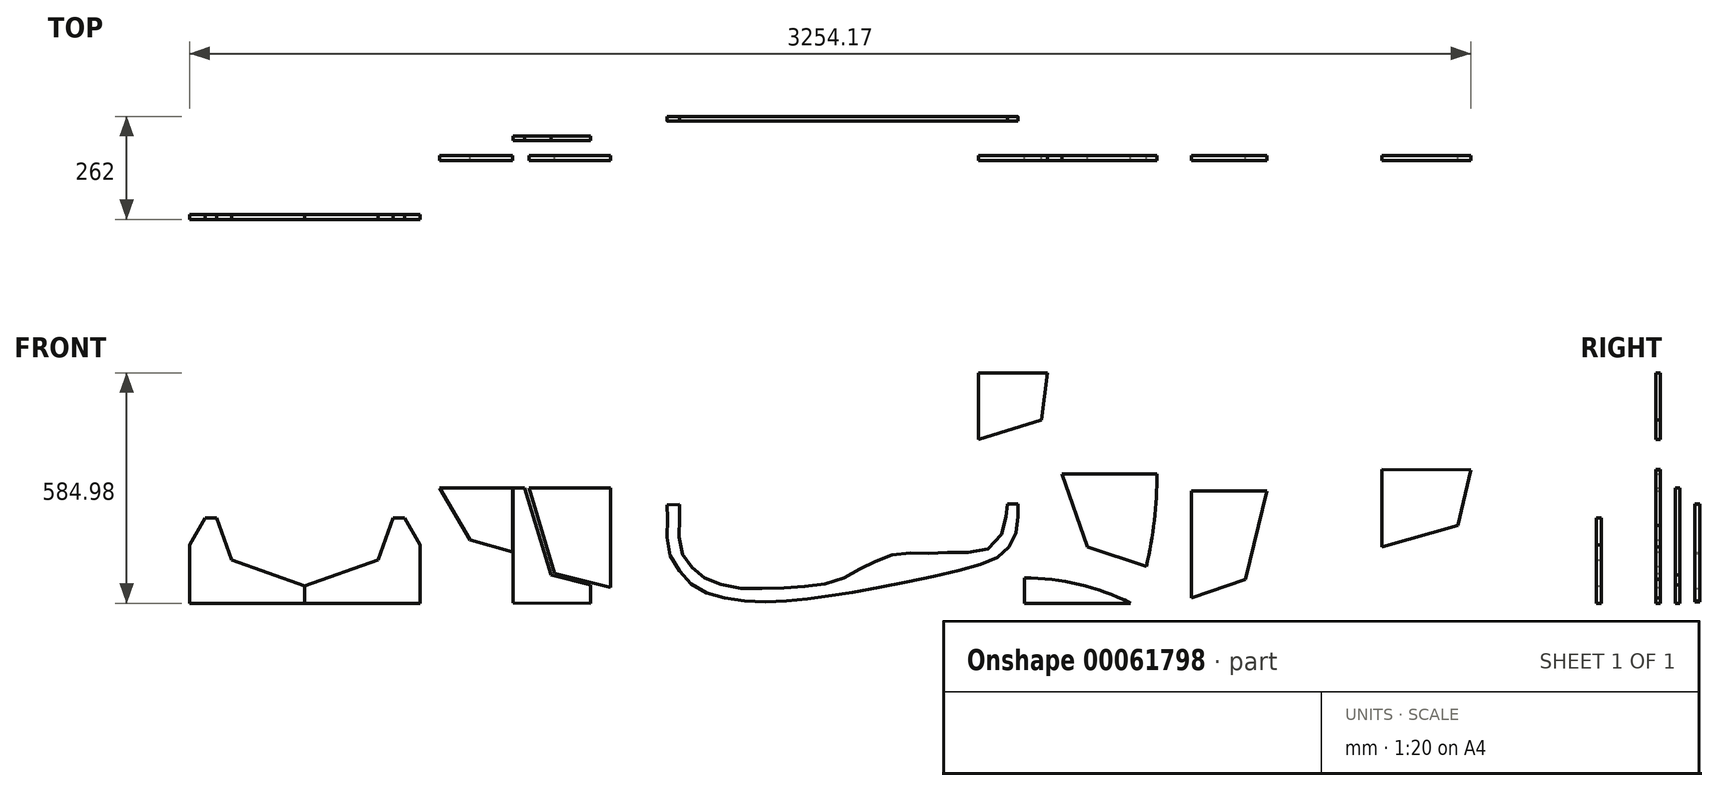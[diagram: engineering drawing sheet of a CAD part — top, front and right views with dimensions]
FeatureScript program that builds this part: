
annotation { "Feature Type Name" : "Feature", "Feature Type Description" : "" }
export const myFeature = defineFeature(function(context is Context, id is Id, definition is map)
    precondition{}
    {
        {
            var Q0;
            Q0=qCreatedBy(makeId("Front.planeOp"),FACE);
            var sketch = newSketch(context, id + "F0", { "sketchPlane" : qUnion([Q0])});
            skFitSpline(sketch, "E0", {"points": [v(-2243.05, -25.44) * mm, v(-2243.98, -16.42) * mm, v(-2246.04, 3.74) * mm, v(-2251.73, 34.57) * mm, v(-2266.06, 64.55) * mm, v(-2293.47, 88.88) * mm, v(-2331.78, 97.5) * mm, v(-2372.4, 97.43) * mm, v(-2409.6, 97.4) * mm, v(-2443.78, 98.85) * mm, v(-2475.9, 98) * mm, v(-2507.54, 98.78) * mm, v(-2539.43, 102.87) * mm, v(-2567.19, 113.88) * mm, v(-2593.9, 125.33) * mm, v(-2619.6, 138.39) * mm, v(-2646.1, 154.9) * mm, v(-2679.7, 166.64) * mm, v(-2715.61, 176.71) * mm, v(-2755.29, 181.36) * mm, v(-2796.14, 183.32) * mm, v(-2840.6, 186.3) * mm, v(-2884.66, 185.2) * mm, v(-2926.7, 185.18) * mm, v(-2964.32, 176.66) * mm, v(-2996.14, 167.64) * mm, v(-3021.51, 153.5) * mm, v(-3040.18, 137.61) * mm, v(-3054.54, 117.9) * mm, v(-3069.45, 97.34) * mm, v(-3077.28, 68.64) * mm, v(-3077.17, 34.43) * mm, v(-3076.08, 1.24) * mm, v(-3075.87, -20.2) * mm, v(-3075.79, -28.7) * mm]});
            skFitSpline(sketch, "E1", {"points": [v(-3106.85, -28.36) * mm, v(-3106.9, -20.44) * mm, v(-3107.02, 0.37) * mm, v(-3106.23, 31.69) * mm, v(-3108.31, 64.14) * mm, v(-3102.94, 93.46) * mm, v(-3090.77, 119.35) * mm, v(-3074.24, 143.6) * mm, v(-3056.37, 165.93) * mm, v(-3033.66, 182.62) * mm, v(-3008.83, 196.33) * mm, v(-2979, 205.88) * mm, v(-2944.71, 211.74) * mm, v(-2906.9, 217.31) * mm, v(-2868.34, 219.82) * mm, v(-2828.97, 218.22) * mm, v(-2789.58, 217.82) * mm, v(-2750, 212.56) * mm, v(-2710.29, 207.3) * mm, v(-2660.36, 200.6) * mm, v(-2601.7, 191.4) * mm, v(-2530.97, 177.85) * mm, v(-2463.88, 164.78) * mm, v(-2399.77, 150.4) * mm, v(-2347.33, 138.38) * mm, v(-2306.06, 126) * mm, v(-2276.88, 114.24) * mm, v(-2255.8, 102.32) * mm, v(-2242.01, 87.43) * mm, v(-2230.57, 71.2) * mm, v(-2221.96, 50.11) * mm, v(-2216.99, 25.98) * mm, v(-2216.73, -0.15) * mm, v(-2216.48, -16.5) * mm, v(-2216.34, -25.35) * mm]});
            skLineSegment(sketch, "E2", {"start": v(-2243.05, -25.44) * mm, "end": v(-2216.34, -25.35) * mm});
            skFitSpline(sketch, "E3", {"points": [v(-2243.05, -25.44) * mm, v(-2243.92, -34.46) * mm, v(-2245.85, -54.63) * mm, v(-2251.34, -85.5) * mm, v(-2265.47, -115.57) * mm, v(-2292.73, -140.08) * mm, v(-2330.98, -148.96) * mm, v(-2371.6, -149.14) * mm, v(-2408.8, -149.35) * mm, v(-2442.96, -151.02) * mm, v(-2475.1, -150.38) * mm, v(-2506.73, -151.37) * mm, v(-2538.59, -155.66) * mm, v(-2566.28, -166.86) * mm, v(-2592.9, -178.47) * mm, v(-2618.54, -191.7) * mm, v(-2644.93, -208.4) * mm, v(-2678.45, -220.34) * mm, v(-2714.3, -230.65) * mm, v(-2753.93, -235.55) * mm, v(-2794.77, -237.78) * mm, v(-2839.22, -241.05) * mm, v(-2883.28, -240.24) * mm, v(-2925.32, -240.48) * mm, v(-2963, -232.2) * mm, v(-2994.87, -223.4) * mm, v(-3020.34, -209.42) * mm, v(-3039.1, -193.65) * mm, v(-3053.59, -174.03) * mm, v(-3068.64, -153.57) * mm, v(-3076.65, -124.92) * mm, v(-3076.77, -90.71) * mm, v(-3075.9, -57.52) * mm, v(-3075.82, -36.07) * mm, v(-3075.8, -27.58) * mm]});
            skFitSpline(sketch, "E4", {"points": [v(-3106.85, -28.36) * mm, v(-3106.84, -36.2) * mm, v(-3106.83, -56.93) * mm, v(-3105.84, -88.16) * mm, v(-3107.71, -120.62) * mm, v(-3102.15, -149.91) * mm, v(-3089.8, -175.72) * mm, v(-3073.13, -199.87) * mm, v(-3055.1, -222.07) * mm, v(-3032.3, -238.62) * mm, v(-3007.38, -252.17) * mm, v(-2977.5, -261.52) * mm, v(-2943.16, -267.16) * mm, v(-2905.31, -272.49) * mm, v(-2866.73, -274.75) * mm, v(-2827.37, -272.89) * mm, v(-2787.99, -272.23) * mm, v(-2748.44, -266.72) * mm, v(-2708.77, -261.2) * mm, v(-2658.88, -254.18) * mm, v(-2600.29, -244.6) * mm, v(-2529.65, -230.59) * mm, v(-2462.65, -217.08) * mm, v(-2398.62, -202.29) * mm, v(-2346.26, -189.92) * mm, v(-2305.08, -177.28) * mm, v(-2275.98, -165.33) * mm, v(-2254.96, -153.28) * mm, v(-2241.28, -138.3) * mm, v(-2229.94, -121.98) * mm, v(-2221.47, -100.85) * mm, v(-2216.66, -76.68) * mm, v(-2216.56, -50.55) * mm, v(-2216.42, -34.2) * mm, v(-2216.34, -25.35) * mm]});
            skLineSegment(sketch, "E5", {"start": v(-3106.85, -28.24) * mm, "end": v(-3106.85, -28.36) * mm});
            skLineSegment(sketch, "E6", {"start": v(-3075.8, -28.14) * mm, "end": v(-3106.85, -28.24) * mm});
            skFitSpline(sketch, "E7", {"points": [v(-2118.13, -166.73) * mm, v(-2132.6, -165.65) * mm, v(-2163.36, -163.34) * mm, v(-2179.13, -136.51) * mm, v(-2187.5, -122.3) * mm]});
            skLineSegment(sketch, "E8", {"start": v(-2187.5, -122.3) * mm, "end": v(-2223.52, 127.42) * mm});
            skFitSpline(sketch, "E9", {"points": [v(-2223.52, 127.42) * mm, v(-2224.23, 132.93) * mm, v(-2226, 146.5) * mm, v(-2208.7, 163.68) * mm, v(-2183.27, 173.92) * mm, v(-2148.18, 166.6) * mm, v(-2133.18, 134.42) * mm, v(-2123.45, 113.8) * mm, v(-2121.76, 103.7) * mm]});
            skLineSegment(sketch, "E10", {"start": v(-2121.06, 96.9) * mm, "end": v(-2118.13, -166.73) * mm});
            skLineSegment(sketch, "E11", {"start": v(-2215.07, 72.49) * mm, "end": v(-2191.1, 76.68) * mm});
            skLineSegment(sketch, "E12", {"start": v(-2121.06, 96.9) * mm, "end": v(-2159.56, 113.17) * mm});
            skLineSegment(sketch, "E13", {"start": v(-3587.98, 306.96) * mm, "end": v(-3517.12, 274.88) * mm});
            skLineSegment(sketch, "E14", {"start": v(-3517.12, 274.88) * mm, "end": v(-3517.23, 240.88) * mm});
            skLineSegment(sketch, "E15", {"start": v(-3517.23, 240.88) * mm, "end": v(-3626.36, 201.24) * mm});
            skLineSegment(sketch, "E16", {"start": v(-3626.36, 201.24) * mm, "end": v(-3690.99, 14.46) * mm});
            skLineSegment(sketch, "E17", {"start": v(-3690.99, 14.46) * mm, "end": v(-3625.6, -171.76) * mm});
            skLineSegment(sketch, "E18", {"start": v(-3625.6, -171.76) * mm, "end": v(-3518.74, -210.12) * mm});
            skLineSegment(sketch, "E19", {"start": v(-3518.74, -210.12) * mm, "end": v(-3518.83, -239.12) * mm});
            skLineSegment(sketch, "E20", {"start": v(-3518.83, -239.12) * mm, "end": v(-3587, -278.04) * mm});
            skLineSegment(sketch, "E21", {"start": v(-3587, -278.04) * mm, "end": v(-3735, -278.04) * mm});
            skLineSegment(sketch, "E22", {"start": v(-3735, -278.04) * mm, "end": v(-3735, 306.96) * mm});
            skLineSegment(sketch, "E23", {"start": v(-3301.27, 306.96) * mm, "end": v(-3300.34, 262.64) * mm});
            skLineSegment(sketch, "E24", {"start": v(-3300.34, 262.64) * mm, "end": v(-3402.47, 236.14) * mm});
            skLineSegment(sketch, "E25", {"start": v(-3402.47, 236.14) * mm, "end": v(-3469.54, 14.46) * mm});
            skLineSegment(sketch, "E26", {"start": v(-3469.54, 14.46) * mm, "end": v(-3401.6, -206.87) * mm});
            skLineSegment(sketch, "E27", {"start": v(-3401.6, -206.87) * mm, "end": v(-3301.73, -231.36) * mm});
            skLineSegment(sketch, "E28", {"start": v(-3301.73, -231.36) * mm, "end": v(-3301.02, -278.04) * mm});
            skLineSegment(sketch, "E29", {"start": v(-3281.23, -278.04) * mm, "end": v(-3479.22, -278.04) * mm});
            skLineSegment(sketch, "E30", {"start": v(-3499.02, -278.04) * mm, "end": v(-3499.08, 306.96) * mm});
            skLineSegment(sketch, "E31", {"start": v(-3499.36, 177.32) * mm, "end": v(-3499.36, -147.69) * mm});
            skLineSegment(sketch, "E32", {"start": v(-3685.36, 14.46) * mm, "end": v(-3607.55, 146.98) * mm});
            skLineSegment(sketch, "E33", {"start": v(-3607.55, 146.98) * mm, "end": v(-3499.36, 177.32) * mm});
            skLineSegment(sketch, "E34", {"start": v(-1775.17, -264.74) * mm, "end": v(-1775.34, 276.26) * mm});
            skLineSegment(sketch, "E35", {"start": v(-1775.17, 279.14) * mm, "end": v(-1637.58, 231.47) * mm});
            skLineSegment(sketch, "E36", {"start": v(-1637.58, 231.47) * mm, "end": v(-1583.68, 7.2) * mm});
            skLineSegment(sketch, "E37", {"start": v(-2140.91, 306.94) * mm, "end": v(-2156.26, 187.98) * mm});
            skLineSegment(sketch, "E38", {"start": v(-2156.26, 187.98) * mm, "end": v(-2316.42, 137.46) * mm});
            skLineSegment(sketch, "E39", {"start": v(-1889.69, -184.8) * mm, "end": v(-2039, -135.3) * mm});
            skLineSegment(sketch, "E40", {"start": v(-2039, -135.3) * mm, "end": v(-2104.67, 50.15) * mm});
            skLineSegment(sketch, "E41", {"start": v(-2104.67, 50.15) * mm, "end": v(-2040.02, 236.76) * mm});
            skLineSegment(sketch, "E42", {"start": v(-2040.02, 236.76) * mm, "end": v(-1891.84, 291.48) * mm});
            skArc(sketch, "E43", {"start": v(-1889.69, -184.8) * mm, "mid": v(-1798.62, 53.76) * mm, "end": v(-1891.84, 291.48) * mm});
            skLineSegment(sketch, "E44", {"start": v(-3250.27, 267.57) * mm, "end": v(-3250.27, -237.5) * mm});
            skLineSegment(sketch, "E45", {"start": v(-3250.27, -237.5) * mm, "end": v(-3392.94, -202.5) * mm});
            skLineSegment(sketch, "E46", {"start": v(-3392.94, -202.5) * mm, "end": v(-3457.54, 14.46) * mm});
            skLineSegment(sketch, "E47", {"start": v(-3457.54, 14.46) * mm, "end": v(-3392.94, 231.11) * mm});
            skLineSegment(sketch, "E48", {"start": v(-3392.94, 231.11) * mm, "end": v(-3250.27, 267.57) * mm});
            skLineSegment(sketch, "E49", {"start": v(-1516.22, 61.56) * mm, "end": v(-1065.83, 60.97) * mm});
            skLineSegment(sketch, "E50", {"start": v(-1065.83, 60.97) * mm, "end": v(-1098.65, -80.85) * mm});
            skLineSegment(sketch, "E51", {"start": v(-1098.65, -80.85) * mm, "end": v(-1290.96, -134.75) * mm});
            skLineSegment(sketch, "E52", {"start": v(-3113.03, 106.96) * mm, "end": v(-3113.03, -278.04) * mm});
            skLineSegment(sketch, "E53", {"start": v(-3113.03, -278.04) * mm, "end": v(-3250.03, -278.04) * mm});
            skLineSegment(sketch, "E54", {"start": v(-3250.03, -278.04) * mm, "end": v(-3250.03, 106.96) * mm});
            skLineSegment(sketch, "E55", {"start": v(-3250.03, 106.96) * mm, "end": v(-3248.8, 303.96) * mm});
            skLineSegment(sketch, "E56", {"start": v(-3248.8, 303.96) * mm, "end": v(-3125.13, 282.94) * mm});
            skLineSegment(sketch, "E57", {"start": v(-3125.13, 282.94) * mm, "end": v(-3124.01, 106.9) * mm});
            skLineSegment(sketch, "E58", {"start": v(-3124.01, 106.9) * mm, "end": v(-3250.03, 106.96) * mm});
            skFitSpline(sketch, "E59", {"points": [v(-3021.64, -29.03) * mm, v(-3021.2, -69.2) * mm, v(-3020.56, -125.45) * mm, v(-2972.02, -206.62) * mm, v(-2881.38, -231.82) * mm, v(-2778.78, -224.88) * mm, v(-2675.77, -198.65) * mm, v(-2588.1, -154.63) * mm, v(-2538.66, -103.43) * mm, v(-2516.98, -61.68) * mm, v(-2515.58, -39.4) * mm, v(-2514.66, -24.67) * mm]});
            skFitSpline(sketch, "E60", {"points": [v(-3021.64, -29.03) * mm, v(-3021.88, 11.15) * mm, v(-3022.22, 67.4) * mm, v(-2975.07, 149.39) * mm, v(-2884.88, 176.14) * mm, v(-2782.18, 170.97) * mm, v(-2678.73, 146.51) * mm, v(-2590.32, 104) * mm, v(-2540, 53.66) * mm, v(-2517.61, 12.29) * mm, v(-2515.84, -9.97) * mm, v(-2514.66, -24.67) * mm]});
            skFitSpline(sketch, "E61", {"points": [v(-3046.82, -29.24) * mm, v(-3046.32, -73.39) * mm, v(-3045.63, -135.18) * mm, v(-2992.3, -224.35) * mm, v(-2892.72, -252.03) * mm, v(-2780, -244.41) * mm, v(-2666.83, -215.6) * mm, v(-2570.52, -167.23) * mm, v(-2516.2, -110.99) * mm, v(-2492.39, -65.12) * mm, v(-2490.85, -40.64) * mm, v(-2489.84, -24.46) * mm]});
            skFitSpline(sketch, "E62", {"points": [v(-3046.82, -29.24) * mm, v(-3047.08, 14.9) * mm, v(-3047.45, 76.7) * mm, v(-2995.66, 166.77) * mm, v(-2896.57, 196.16) * mm, v(-2783.74, 190.47) * mm, v(-2670.09, 163.6) * mm, v(-2572.96, 116.9) * mm, v(-2517.69, 61.6) * mm, v(-2493.08, 16.15) * mm, v(-2491.13, -8.3) * mm, v(-2489.84, -24.46) * mm]});
            skLineSegment(sketch, "E63", {"start": v(-3046.82, -29.24) * mm, "end": v(-3021.64, -29.03) * mm});
            skArc(sketch, "E64", {"start": v(-1889.69, -184.8) * mm, "mid": v(-1862.92, 53.42) * mm, "end": v(-1892.21, 291.35) * mm});
            skLineSegment(sketch, "E65", {"start": v(-3735, 306.96) * mm, "end": v(-1695, 306.96) * mm});
            skLineSegment(sketch, "E66", {"start": v(-2514.66, -24.67) * mm, "end": v(-2489.84, -24.46) * mm});
            skLineSegment(sketch, "E67", {"start": v(-2491.96, 305.02) * mm, "end": v(-2991.96, 305.02) * mm});
            skLineSegment(sketch, "E68", {"start": v(-2991.96, 305.02) * mm, "end": v(-2991.96, 255.02) * mm});
            skLineSegment(sketch, "E69", {"start": v(-1695, -278.04) * mm, "end": v(-3735, -278.04) * mm});
            skArc(sketch, "E70", {"start": v(-1929.84, -278.04) * mm, "mid": v(-2199.84, -167.1) * mm, "end": v(-2469.84, -278.04) * mm});
            skArc(sketch, "E71", {"start": v(-1929.84, -278.04) * mm, "mid": v(-2199.84, -213.86) * mm, "end": v(-2469.84, -278.04) * mm});
            skLineSegment(sketch, "E72", {"start": v(-3113.03, -158.04) * mm, "end": v(-3138.91, -158.04) * mm});
            skLineSegment(sketch, "E73", {"start": v(-3193.03, -198.04) * mm, "end": v(-3203.03, -198.04) * mm});
            skLineSegment(sketch, "E74", {"start": v(-3198.03, -203.04) * mm, "end": v(-3198.03, -193.04) * mm});
            skCircle(sketch, "E75", {"center": v(-3198.03, -198.04) * mm, "radius": 5 * mm});
            skFitSpline(sketch, "E76", {"points": [v(-3234.84, 85.11) * mm, v(-3220.4, 83.85) * mm, v(-3189.65, 81.16) * mm, v(-3174.21, 54.14) * mm, v(-3166.03, 39.82) * mm]});
            skLineSegment(sketch, "E77", {"start": v(-3166.03, 39.82) * mm, "end": v(-3133.08, -210.32) * mm});
            skFitSpline(sketch, "E78", {"points": [v(-3133.08, -210.32) * mm, v(-3132.43, -215.83) * mm, v(-3130.84, -229.42) * mm, v(-3148.34, -246.4) * mm, v(-3173.9, -256.32) * mm, v(-3208.9, -248.56) * mm, v(-3224, -215.06) * mm, v(-3235.93, -188.99) * mm, v(-3235.13, -172.6) * mm, v(-3234.9, -167.89) * mm]});
            skLineSegment(sketch, "E79", {"start": v(-3234.9, -167.89) * mm, "end": v(-3234.84, 85.11) * mm});
            skCircle(sketch, "E80", {"center": v(-2158.42, 115.95) * mm, "radius": 3 * mm});
            skLineSegment(sketch, "E81", {"start": v(-2121.76, 103.7) * mm, "end": v(-2157.28, 118.72) * mm});
            skLineSegment(sketch, "E82", {"start": v(-2158.42, 115.95) * mm, "end": v(-2159.38, 118.8) * mm});
            skLineSegment(sketch, "E83", {"start": v(-2159.38, 118.8) * mm, "end": v(-2158.42, 115.95) * mm});
            skLineSegment(sketch, "E84", {"start": v(-2158.42, 115.95) * mm, "end": v(-2157.46, 113.1) * mm});
            skLineSegment(sketch, "E85", {"start": v(-2157.46, 113.1) * mm, "end": v(-2158.42, 115.95) * mm});
            skLineSegment(sketch, "E86", {"start": v(-2158.42, 115.95) * mm, "end": v(-2161.26, 114.99) * mm});
            skLineSegment(sketch, "E87", {"start": v(-2161.26, 114.99) * mm, "end": v(-2158.42, 115.95) * mm});
            skLineSegment(sketch, "E88", {"start": v(-2158.42, 115.95) * mm, "end": v(-2155.58, 116.9) * mm});
            skLineSegment(sketch, "E89", {"start": v(-3250.03, 106.96) * mm, "end": v(-3113.03, 106.96) * mm});
            skLineSegment(sketch, "E90", {"start": v(-2491.96, 305.02) * mm, "end": v(-2491.96, 264.57) * mm});
            skFitSpline(sketch, "E91", {"points": [v(-1683.92, 291.86) * mm, v(-1647.43, 267.6) * mm, v(-1578.86, 222.03) * mm, v(-1477.55, 160.36) * mm, v(-1402, 129.5) * mm, v(-1361.26, 116.83) * mm, v(-1354.92, 114.86) * mm]});
            skFitSpline(sketch, "E92", {"points": [v(-1354.92, 114.86) * mm, v(-1327.92, 114.14) * mm, v(-1234.27, 111.67) * mm, v(-1073.9, 110.34) * mm, v(-873.92, 105.8) * mm, v(-673.93, 101.6) * mm, v(-473.91, 98.98) * mm, v(-273.92, 95.65) * mm, v(-73.89, 93.59) * mm, v(126.06, 87.15) * mm, v(292.11, 85.34) * mm, v(458.73, 79.4) * mm, v(625.47, 77.02) * mm, v(826.01, 67.34) * mm, v(1026.1, 66.83) * mm, v(1226.05, 60.51) * mm, v(1426.09, 62.27) * mm, v(1626.08, 61.55) * mm, v(1826.09, 62.67) * mm, v(2026.08, 64.93) * mm, v(2226.08, 66.77) * mm, v(2426.08, 69.14) * mm, v(2626.12, 69.8) * mm, v(2826.05, 76.78) * mm, v(3018.77, 78.17) * mm, v(3144.75, 81.36) * mm, v(3204.08, 82.86) * mm]});
            skLineSegment(sketch, "E93", {"start": v(3204.08, 82.86) * mm, "end": v(3717.08, 272.86) * mm});
            skFitSpline(sketch, "E94", {"points": [v(-1683.92, 291.86) * mm, v(-1647.27, 287.36) * mm, v(-1577.37, 278.77) * mm, v(-1473.95, 268.82) * mm, v(-1374, 259.47) * mm, v(-1240.71, 250.15) * mm, v(-1073.96, 244.28) * mm, v(-873.93, 240.72) * mm, v(-673.92, 237.98) * mm, v(-473.92, 234.51) * mm, v(-273.91, 233.12) * mm, v(-73.92, 230.16) * mm, v(126.09, 231.39) * mm, v(326.08, 229.44) * mm, v(526.08, 230.02) * mm, v(726.09, 229.64) * mm, v(926.08, 230.56) * mm, v(1126.1, 233.27) * mm, v(1326.08, 227.52) * mm, v(1526.08, 223.79) * mm, v(1726.12, 220.48) * mm, v(1926.06, 213.45) * mm, v(2126.08, 208.88) * mm, v(2326.06, 204.2) * mm, v(2526.09, 203.47) * mm, v(2720.8, 205.02) * mm, v(2887.5, 210.17) * mm, v(3054.06, 219.7) * mm, v(3192.84, 225.23) * mm, v(3326.17, 234.47) * mm, v(3489.83, 249.73) * mm, v(3620.1, 262.99) * mm, v(3717.08, 272.86) * mm]});
            skFitSpline(sketch, "E95", {"points": [v(-1453.62, -178.53) * mm, v(-1433.67, -185.01) * mm, v(-1397.35, -196.82) * mm, v(-1344.25, -211.67) * mm, v(-1277.2, -220.23) * mm, v(-1193.6, -221.95) * mm, v(-1093.67, -227.48) * mm, v(-993.6, -227.3) * mm, v(-860.29, -228.9) * mm, v(-726.95, -230.88) * mm, v(-560.28, -230.2) * mm, v(-393.6, -232.5) * mm, v(-193.61, -235.45) * mm, v(6.38, -238.87) * mm, v(206.39, -240.25) * mm, v(406.38, -243.3) * mm, v(606.39, -241.71) * mm, v(806.4, -245.03) * mm, v(1006.37, -239.36) * mm, v(1206.39, -240.72) * mm, v(1406.39, -240.93) * mm, v(1606.4, -238.74) * mm, v(1806.38, -235.28) * mm, v(2006.38, -233.3) * mm, v(2206.39, -232.69) * mm, v(2373.07, -231.4) * mm, v(2506.4, -228.55) * mm, v(2606.48, -226.31) * mm, v(2706.62, -219.36) * mm, v(2806.74, -207.3) * mm, v(2906.87, -190.33) * mm, v(2997.36, -170.15) * mm, v(3054.4, -155.63) * mm, v(3078.38, -149.53) * mm]});
            skFitSpline(sketch, "E96", {"points": [v(-1453.62, -178.53) * mm, v(-1400.3, -173.75) * mm, v(-1313.64, -165.98) * mm, v(-1193.4, -156.48) * mm, v(-1093.74, -142.81) * mm, v(-993.37, -133.47) * mm, v(-860.39, -113.38) * mm, v(-694.01, -90.19) * mm, v(-493.67, -70.6) * mm, v(-293.8, -50.65) * mm, v(-93.7, -36.07) * mm, v(106.3, -24.28) * mm, v(306.28, -14) * mm, v(506.39, -12.93) * mm, v(706.38, -9.47) * mm, v(906.4, -12.37) * mm, v(1106.5, -16.25) * mm, v(1306.37, -27.85) * mm, v(1506.38, -37.53) * mm, v(1706.44, -47.2) * mm, v(1906.5, -58.9) * mm, v(2106.42, -74.45) * mm, v(2306.39, -90.51) * mm, v(2506.35, -106.68) * mm, v(2706.33, -121.92) * mm, v(2897.15, -134.22) * mm, v(3021.06, -144.69) * mm, v(3078.38, -149.53) * mm]});
            skLineSegment(sketch, "E97", {"start": v(327.38, -242.53) * mm, "end": v(327.38, -169.52) * mm});
            skLineSegment(sketch, "E98", {"start": v(3725.24, -204.64) * mm, "end": v(3725.24, 295.36) * mm});
            skLineSegment(sketch, "E99", {"start": v(3646.25, -253.66) * mm, "end": v(3146.25, -253.66) * mm});
            skLineSegment(sketch, "E100", {"start": v(3725.24, -204.64) * mm, "end": v(3675.24, -204.64) * mm});
            skLineSegment(sketch, "E101", {"start": v(3146.25, -213.2) * mm, "end": v(3146.25, -253.66) * mm});
            skLineSegment(sketch, "E102", {"start": v(3646.25, -213.2) * mm, "end": v(3646.25, -253.66) * mm});
            skLineSegment(sketch, "E103", {"start": v(3725.24, 295.36) * mm, "end": v(3684.56, 295.36) * mm});
            skLineSegment(sketch, "E104", {"start": v(-1695, 306.96) * mm, "end": v(3735, 306.96) * mm});
            skLineSegment(sketch, "E105", {"start": v(3735, 306.96) * mm, "end": v(3735, -278.04) * mm});
            skLineSegment(sketch, "E106", {"start": v(-1695, -278.04) * mm, "end": v(3735, -278.04) * mm});
            skFitSpline(sketch, "E107", {"points": [v(-1572.01, 218.65) * mm, v(-1539.34, 215.11) * mm, v(-1473.32, 208.76) * mm, v(-1374, 199.47) * mm, v(-1240.71, 190.15) * mm, v(-1073.96, 184.28) * mm, v(-873.93, 180.72) * mm, v(-673.92, 177.98) * mm, v(-473.92, 174.51) * mm, v(-273.91, 173.12) * mm, v(-73.92, 170.16) * mm, v(126.09, 171.39) * mm, v(326.08, 169.44) * mm, v(526.08, 170.02) * mm, v(726.09, 169.64) * mm, v(926.08, 170.56) * mm, v(1126.1, 173.27) * mm, v(1326.08, 167.52) * mm, v(1526.08, 163.79) * mm, v(1726.12, 160.48) * mm, v(1926.06, 153.45) * mm, v(2126.08, 148.88) * mm, v(2326.06, 144.2) * mm, v(2526.09, 143.47) * mm, v(2720.8, 145.02) * mm, v(2887.5, 150.17) * mm, v(3054.06, 159.7) * mm, v(3192.84, 165.23) * mm, v(3326.17, 174.47) * mm, v(3415.66, 182.81) * mm, v(3471.85, 188.26) * mm, v(3494.73, 190.5) * mm]});
            skFitSpline(sketch, "E108", {"points": [v(-2958.87, -25.9) * mm, v(-2957.85, -5.92) * mm, v(-2955.23, 45.3) * mm, v(-2947.8, 110.6) * mm, v(-2918.5, 164.73) * mm, v(-2888.4, 188.06) * mm, v(-2859.34, 196.73) * mm, v(-2839.31, 201.13) * mm, v(-2819.37, 204.62) * mm, v(-2799.4, 207.18) * mm, v(-2779.38, 208.33) * mm, v(-2759.45, 210.04) * mm, v(-2739.37, 210.9) * mm, v(-2719.4, 208.6) * mm, v(-2699.2, 207.8) * mm, v(-2679.03, 204.02) * mm, v(-2658.79, 198.56) * mm, v(-2638.76, 190.8) * mm, v(-2618.55, 182.28) * mm, v(-2598.04, 172.88) * mm, v(-2577.79, 161.18) * mm, v(-2557.11, 147.68) * mm, v(-2536.6, 130.79) * mm, v(-2513.35, 108.8) * mm, v(-2485.75, 61.05) * mm, v(-2478.84, 16.62) * mm, v(-2474.01, -14.39) * mm]});
            skFitSpline(sketch, "E109", {"points": [v(-2978.96, -26.14) * mm, v(-2977.85, -4.5) * mm, v(-2975.01, 50.95) * mm, v(-2966.98, 121.62) * mm, v(-2935.25, 180.22) * mm, v(-2902.66, 205.48) * mm, v(-2871.21, 214.87) * mm, v(-2849.54, 219.63) * mm, v(-2827.95, 223.4) * mm, v(-2806.33, 226.17) * mm, v(-2784.66, 227.42) * mm, v(-2763.08, 229.27) * mm, v(-2741.34, 230.2) * mm, v(-2719.73, 227.7) * mm, v(-2697.85, 226.85) * mm, v(-2676.03, 222.76) * mm, v(-2654.1, 216.86) * mm, v(-2624.95, 205.47) * mm, v(-2595.25, 192.94) * mm, v(-2566.43, 176.4) * mm, v(-2544.05, 161.76) * mm, v(-2521.85, 143.48) * mm, v(-2496.68, 119.67) * mm, v(-2466.8, 68) * mm, v(-2459.32, 19.9) * mm, v(-2454.1, -13.67) * mm]});
            skFitSpline(sketch, "E110", {"points": [v(-2958.89, -25.42) * mm, v(-2956.91, -45.33) * mm, v(-2951.86, -96.38) * mm, v(-2941.35, -161.24) * mm, v(-2909.5, -213.93) * mm, v(-2878.32, -235.8) * mm, v(-2848.9, -243.09) * mm, v(-2828.68, -246.53) * mm, v(-2808.6, -249.06) * mm, v(-2788.53, -250.67) * mm, v(-2768.47, -250.87) * mm, v(-2748.48, -251.63) * mm, v(-2728.38, -251.54) * mm, v(-2708.55, -248.29) * mm, v(-2688.4, -246.54) * mm, v(-2668.44, -241.8) * mm, v(-2648.48, -235.4) * mm, v(-2628.85, -226.68) * mm, v(-2609.06, -217.21) * mm, v(-2589.02, -206.85) * mm, v(-2569.35, -194.2) * mm, v(-2549.33, -179.73) * mm, v(-2529.65, -161.9) * mm, v(-2507.47, -138.82) * mm, v(-2482.17, -89.82) * mm, v(-2477.37, -45.11) * mm, v(-2474.02, -13.9) * mm]});
            skFitSpline(sketch, "E111", {"points": [v(-2978.96, -26.14) * mm, v(-2976.83, -47.7) * mm, v(-2971.36, -102.96) * mm, v(-2959.98, -173.16) * mm, v(-2925.5, -230.2) * mm, v(-2891.75, -253.87) * mm, v(-2859.9, -261.76) * mm, v(-2838.01, -265.49) * mm, v(-2816.27, -268.23) * mm, v(-2794.55, -269.98) * mm, v(-2772.84, -270.19) * mm, v(-2751.2, -271.01) * mm, v(-2729.44, -270.91) * mm, v(-2707.97, -267.4) * mm, v(-2686.16, -265.5) * mm, v(-2664.55, -260.38) * mm, v(-2642.95, -253.43) * mm, v(-2621.7, -244) * mm, v(-2600.27, -233.76) * mm, v(-2578.58, -222.54) * mm, v(-2557.28, -208.85) * mm, v(-2535.62, -193.18) * mm, v(-2514.31, -173.87) * mm, v(-2490.3, -148.9) * mm, v(-2462.91, -95.85) * mm, v(-2457.72, -47.46) * mm, v(-2454.1, -13.67) * mm]});
            skFitSpline(sketch, "E112", {"points": [v(-1666.66, 280.4) * mm, v(-1634.9, 276.5) * mm, v(-1569.89, 268.63) * mm, v(-1471.38, 259.15) * mm, v(-1371.43, 249.8) * mm, v(-1238.14, 240.48) * mm, v(-1071.4, 234.61) * mm, v(-871.36, 231.06) * mm, v(-671.35, 228.31) * mm, v(-471.36, 224.85) * mm, v(-271.35, 223.45) * mm, v(-71.35, 220.5) * mm, v(128.65, 221.72) * mm, v(328.65, 219.77) * mm, v(528.65, 220.35) * mm, v(728.65, 219.98) * mm, v(928.65, 220.9) * mm, v(1128.68, 223.6) * mm, v(1328.65, 217.86) * mm, v(1528.65, 214.12) * mm, v(1728.68, 210.81) * mm, v(1928.63, 203.79) * mm, v(2128.64, 199.21) * mm, v(2328.63, 194.54) * mm, v(2528.66, 193.8) * mm, v(2723.36, 195.36) * mm, v(2890.06, 200.5) * mm, v(3056.63, 210.05) * mm, v(3195.41, 215.56) * mm, v(3328.74, 224.8) * mm, v(3479.21, 238.84) * mm, v(3596.33, 250.66) * mm, v(3680.14, 259.17) * mm]});
            skFitSpline(sketch, "E113", {"points": [v(-1646.96, 267.34) * mm, v(-1622.63, 264.39) * mm, v(-1565.02, 257.58) * mm, v(-1473.95, 248.82) * mm, v(-1374, 239.47) * mm, v(-1240.71, 230.15) * mm, v(-1073.96, 224.28) * mm, v(-873.93, 220.72) * mm, v(-673.92, 217.98) * mm, v(-473.92, 214.51) * mm, v(-273.91, 213.12) * mm, v(-73.92, 210.16) * mm, v(126.09, 211.39) * mm, v(326.08, 209.44) * mm, v(526.08, 210.02) * mm, v(726.09, 209.64) * mm, v(926.08, 210.56) * mm, v(1126.1, 213.27) * mm, v(1326.08, 207.52) * mm, v(1526.08, 203.79) * mm, v(1726.12, 200.48) * mm, v(1926.06, 193.45) * mm, v(2126.08, 188.88) * mm, v(2326.06, 184.2) * mm, v(2526.09, 183.47) * mm, v(2720.8, 185.02) * mm, v(2887.5, 190.17) * mm, v(3054.06, 199.7) * mm, v(3192.84, 205.23) * mm, v(3326.17, 214.47) * mm, v(3465, 227.42) * mm, v(3570.49, 237.98) * mm, v(3642.66, 245.3) * mm]});
            skFitSpline(sketch, "E114", {"points": [v(-1628.4, 255.1) * mm, v(-1610.25, 252.94) * mm, v(-1558.81, 246.98) * mm, v(-1473.95, 238.82) * mm, v(-1374, 229.47) * mm, v(-1240.71, 220.15) * mm, v(-1073.96, 214.28) * mm, v(-873.93, 210.72) * mm, v(-673.92, 207.98) * mm, v(-473.92, 204.51) * mm, v(-273.91, 203.12) * mm, v(-73.92, 200.16) * mm, v(126.09, 201.39) * mm, v(326.08, 199.44) * mm, v(526.08, 200.02) * mm, v(726.09, 199.64) * mm, v(926.08, 200.56) * mm, v(1126.1, 203.27) * mm, v(1326.08, 197.52) * mm, v(1526.08, 193.79) * mm, v(1726.12, 190.48) * mm, v(1926.06, 183.45) * mm, v(2126.08, 178.88) * mm, v(2326.06, 174.2) * mm, v(2526.09, 173.47) * mm, v(2720.8, 175.02) * mm, v(2887.5, 180.17) * mm, v(3054.06, 189.7) * mm, v(3192.84, 195.23) * mm, v(3326.17, 204.47) * mm, v(3452.61, 216.26) * mm, v(3545.73, 225.51) * mm, v(3605.53, 231.54) * mm]});
            skFitSpline(sketch, "E115", {"points": [v(-1609.75, 242.9) * mm, v(-1597.81, 241.51) * mm, v(-1552.58, 236.38) * mm, v(-1473.95, 228.82) * mm, v(-1374, 219.47) * mm, v(-1240.71, 210.15) * mm, v(-1073.96, 204.28) * mm, v(-873.93, 200.72) * mm, v(-673.92, 197.98) * mm, v(-473.92, 194.51) * mm, v(-273.91, 193.12) * mm, v(-73.92, 190.16) * mm, v(126.09, 191.39) * mm, v(326.08, 189.44) * mm, v(526.08, 190.02) * mm, v(726.09, 189.64) * mm, v(926.08, 190.56) * mm, v(1126.1, 193.27) * mm, v(1326.08, 187.52) * mm, v(1526.08, 183.79) * mm, v(1726.12, 180.48) * mm, v(1926.06, 173.45) * mm, v(2126.08, 168.88) * mm, v(2326.06, 164.2) * mm, v(2526.09, 163.47) * mm, v(2720.8, 165.02) * mm, v(2887.5, 170.17) * mm, v(3054.06, 179.7) * mm, v(3192.84, 185.23) * mm, v(3326.17, 194.47) * mm, v(3440.25, 205.1) * mm, v(3521.02, 213.07) * mm, v(3568.47, 217.82) * mm]});
            skFitSpline(sketch, "E116", {"points": [v(-1590.96, 230.75) * mm, v(-1585.28, 230.1) * mm, v(-1546.3, 225.78) * mm, v(-1473.95, 218.82) * mm, v(-1374, 209.47) * mm, v(-1240.71, 200.15) * mm, v(-1073.96, 194.28) * mm, v(-873.93, 190.72) * mm, v(-673.92, 187.98) * mm, v(-473.92, 184.51) * mm, v(-273.91, 183.12) * mm, v(-73.92, 180.16) * mm, v(126.09, 181.39) * mm, v(326.08, 179.44) * mm, v(526.08, 180.02) * mm, v(726.09, 179.64) * mm, v(926.08, 180.56) * mm, v(1126.1, 183.27) * mm, v(1326.08, 177.52) * mm, v(1526.08, 173.79) * mm, v(1726.12, 170.48) * mm, v(1926.06, 163.45) * mm, v(2126.08, 158.88) * mm, v(2326.06, 154.2) * mm, v(2526.09, 153.47) * mm, v(2720.8, 155.02) * mm, v(2887.5, 160.17) * mm, v(3054.06, 169.7) * mm, v(3192.84, 175.23) * mm, v(3326.17, 184.47) * mm, v(3427.93, 193.96) * mm, v(3496.39, 200.65) * mm, v(3531.53, 204.14) * mm]});
            skLineSegment(sketch, "E117", {"start": v(-3685.36, 15.17) * mm, "end": v(-3607.55, -117.35) * mm});
            skLineSegment(sketch, "E118", {"start": v(-3607.55, -117.35) * mm, "end": v(-3499.36, -147.69) * mm});
            skLineSegment(sketch, "E119", {"start": v(-2491.92, 306.94) * mm, "end": v(-2476.57, 187.98) * mm});
            skLineSegment(sketch, "E120", {"start": v(-2476.57, 187.98) * mm, "end": v(-2316.42, 137.46) * mm});
            skLineSegment(sketch, "E121", {"start": v(-2491.92, 306.94) * mm, "end": v(-2140.91, 306.94) * mm});
            skLineSegment(sketch, "E122", {"start": v(-1775.17, -264.74) * mm, "end": v(-1637.58, -217.07) * mm});
            skLineSegment(sketch, "E123", {"start": v(-1637.58, -217.07) * mm, "end": v(-1583.68, 7.2) * mm});
            skLineSegment(sketch, "E124", {"start": v(-1516.22, 61.56) * mm, "end": v(-1483.27, -80.85) * mm});
            skLineSegment(sketch, "E125", {"start": v(-1483.27, -80.85) * mm, "end": v(-1290.96, -134.75) * mm});
            skSolve(sketch);
        }
        {
            var Q0;
            {var subQ2=sQuery(id+"F0.wireOp",EDGE,"E13");Q0=makeQuery(id+"F0.imprint","IMPRINT",FACE,{"disambiguationData":[TD([[makeQuery(id+"F0.imprint","IMPRINT",EDGE,{"derivedFrom":subQ2}),-1.0]])]});}
            cPlane(context, id + "F1", {"entities" : qUnion([Q0]), "cplaneType" : CPlaneType.OFFSET, "offset" : 150 * mm, "width" : 150 * mm, "height" : 150 * mm});
        }
        {
            var Q0;
            Q0=qCreatedBy(id+"F1.planeOp",FACE);
            var sketch = newSketch(context, id + "F2", { "sketchPlane" : qUnion([Q0])});
            skLineSegment(sketch, "E126.0", {"start": v(-3690.99, 14.46) * mm, "end": v(-3625.6, -171.76) * mm});
            skLineSegment(sketch, "E126.1", {"start": v(-3625.6, -171.76) * mm, "end": v(-3518.74, -210.12) * mm});
            skLineSegment(sketch, "E126.2", {"start": v(-3518.74, -210.12) * mm, "end": v(-3518.83, -239.12) * mm});
            skLineSegment(sketch, "E126.3", {"start": v(-3518.83, -239.12) * mm, "end": v(-3587, -278.04) * mm});
            skLineSegment(sketch, "E126.4", {"start": v(-3735, -278.04) * mm, "end": v(-3735, 14.46) * mm});
            skLineSegment(sketch, "E127", {"start": v(-3735, -278.04) * mm, "end": v(-3587, -278.04) * mm});
            skLineSegment(sketch, "E128", {"start": v(-3690.99, 14.46) * mm, "end": v(-3735, 14.46) * mm});
            skPoint(sketch, "E129.1.end.orphan", {"position": v(-3626.36, 201.24) * mm});
            skPoint(sketch, "E129.1.start.orphan", {"position": v(-3517.23, 240.88) * mm});
            skPoint(sketch, "E129.2.start.orphan", {"position": v(-3626.36, 201.24) * mm});
            skPoint(sketch, "E129.0.end.orphan", {"position": v(-3517.23, 240.88) * mm});
            skPoint(sketch, "E129.0.start.orphan", {"position": v(-3517.12, 274.88) * mm});
            skPoint(sketch, "E130.end.orphan", {"position": v(-3587.98, 306.96) * mm});
            skPoint(sketch, "E131.orphan", {"position": v(-3735, 306.96) * mm});
            skLineSegment(sketch, "E132.0", {"start": v(-3685.36, 15.17) * mm, "end": v(-3607.55, -117.35) * mm});
            skLineSegment(sketch, "E133.0", {"start": v(-3607.55, -117.35) * mm, "end": v(-3499.36, -147.69) * mm});
            skLineSegment(sketch, "E134", {"start": v(-3685.36, 15.17) * mm, "end": v(-3499.36, 15.17) * mm});
            skLineSegment(sketch, "E135", {"start": v(-3499.36, 15.17) * mm, "end": v(-3499.36, -147.69) * mm});
            skLineSegment(sketch, "E136.0", {"start": v(-3301.73, -231.36) * mm, "end": v(-3301.02, -278.04) * mm});
            skLineSegment(sketch, "E137.0", {"start": v(-3401.6, -206.87) * mm, "end": v(-3301.73, -231.36) * mm});
            skLineSegment(sketch, "E138.0", {"start": v(-3250.27, -237.5) * mm, "end": v(-3392.94, -202.5) * mm});
            skLineSegment(sketch, "E139.0", {"start": v(-3392.94, -202.5) * mm, "end": v(-3457.54, 14.46) * mm});
            skLineSegment(sketch, "E140.0", {"start": v(-3469.54, 14.46) * mm, "end": v(-3401.6, -206.87) * mm});
            skLineSegment(sketch, "E141", {"start": v(-3469.54, 14.46) * mm, "end": v(-3499.36, 15.17) * mm});
            skLineSegment(sketch, "E142", {"start": v(-3499.36, -278.04) * mm, "end": v(-3301.02, -278.04) * mm});
            skLineSegment(sketch, "E143", {"start": v(-3457.54, 14.46) * mm, "end": v(-3250.27, 14.46) * mm});
            skLineSegment(sketch, "E144", {"start": v(-3250.27, 14.46) * mm, "end": v(-3250.27, -237.5) * mm});
            skLineSegment(sketch, "E145.0", {"start": v(-1892.21, 291.35) * mm, "end": v(-1891.84, 291.48) * mm});
            skArc(sketch, "E146.0", {"start": v(-1889.69, -184.8) * mm, "mid": v(-1869.5, -68.1) * mm, "end": v(-1862.9, 50.15) * mm});
            skLineSegment(sketch, "E147.0", {"start": v(-2039, -135.3) * mm, "end": v(-2104.67, 50.15) * mm});
            skLineSegment(sketch, "E148.0", {"start": v(-1889.69, -184.8) * mm, "end": v(-2039, -135.3) * mm});
            skLineSegment(sketch, "E149", {"start": v(-2104.67, 50.15) * mm, "end": v(-1862.9, 50.15) * mm});
            skPoint(sketch, "E150.orphan", {"position": v(-2040.02, 236.76) * mm});
            skLineSegment(sketch, "E151.0", {"start": v(-1637.58, -217.07) * mm, "end": v(-1583.68, 7.2) * mm});
            skLineSegment(sketch, "E152.0", {"start": v(-1775.17, -264.74) * mm, "end": v(-1637.58, -217.07) * mm});
            skLineSegment(sketch, "E153", {"start": v(-1583.68, 7.2) * mm, "end": v(-1775.17, 7.2) * mm});
            skLineSegment(sketch, "E154", {"start": v(-1775.17, 7.2) * mm, "end": v(-1775.17, -264.74) * mm});
            skLineSegment(sketch, "E155.0", {"start": v(-1290.96, 61.26) * mm, "end": v(-1065.83, 60.97) * mm});
            skLineSegment(sketch, "E156.0", {"start": v(-1098.65, -80.85) * mm, "end": v(-1290.96, -134.75) * mm});
            skLineSegment(sketch, "E157.0", {"start": v(-1065.83, 60.97) * mm, "end": v(-1098.65, -80.85) * mm});
            skLineSegment(sketch, "E158", {"start": v(-1290.96, -134.75) * mm, "end": v(-1290.96, 61.26) * mm});
            skPoint(sketch, "E159.orphan", {"position": v(-1516.22, 61.56) * mm});
            skLineSegment(sketch, "E160.0", {"start": v(-2156.26, 187.98) * mm, "end": v(-2316.42, 137.46) * mm});
            skLineSegment(sketch, "E161.0", {"start": v(-2140.91, 306.94) * mm, "end": v(-2156.26, 187.98) * mm});
            skLineSegment(sketch, "E162", {"start": v(-2316.42, 137.46) * mm, "end": v(-2316.42, 306.94) * mm});
            skLineSegment(sketch, "E163", {"start": v(-2316.42, 306.94) * mm, "end": v(-2140.91, 306.94) * mm});
            skArc(sketch, "E164.0", {"start": v(-1929.84, -278.04) * mm, "mid": v(-2061.08, -230.13) * mm, "end": v(-2199.84, -213.86) * mm});
            skLineSegment(sketch, "E165", {"start": v(-2199.84, -278.04) * mm, "end": v(-1929.84, -278.04) * mm});
            skLineSegment(sketch, "E166", {"start": v(-2199.84, -278.04) * mm, "end": v(-2199.84, -213.86) * mm});
            skPoint(sketch, "E167.orphan", {"position": v(-2469.84, -278.04) * mm});
            skSolve(sketch);
        }
        {
            var Q0;
            Q0 = qSketchRegion(id + "F2", true);
            extrude(context, id + "F3", {"entities" : qUnion([Q0]), "endBound" : BoundingType.SYMMETRIC, "depth" : 12 * mm});
        }
        {
            var Q0;
            {var subQ1=sQuery(id+"F0.wireOp",EDGE,"E23");Q0=makeQuery(id+"F0.imprint","IMPRINT",FACE,{"disambiguationData":[TD([[makeQuery(id+"F0.imprint","IMPRINT",EDGE,{"derivedFrom":subQ1}),-1.0]])]});}
            cPlane(context, id + "F4", {"entities" : qUnion([Q0]), "cplaneType" : CPlaneType.OFFSET, "offset" : 100 * mm, "width" : 150 * mm, "height" : 150 * mm});
        }
        {
            var Q0;
            Q0=qCreatedBy(id+"F4.planeOp",FACE);
            var sketch = newSketch(context, id + "F5", { "sketchPlane" : qUnion([Q0])});
            skLineSegment(sketch, "E168.0", {"start": v(-3469.54, 14.46) * mm, "end": v(-3401.6, -206.87) * mm});
            skLineSegment(sketch, "E169.0", {"start": v(-3401.6, -206.87) * mm, "end": v(-3301.73, -231.36) * mm});
            skLineSegment(sketch, "E170.0", {"start": v(-3301.73, -231.36) * mm, "end": v(-3301.02, -278.04) * mm});
            skLineSegment(sketch, "E171", {"start": v(-3469.54, 14.46) * mm, "end": v(-3499.04, 14.46) * mm});
            skLineSegment(sketch, "E172", {"start": v(-3499.04, 14.46) * mm, "end": v(-3499.04, -277.93) * mm});
            skLineSegment(sketch, "E173", {"start": v(-3499.04, -277.93) * mm, "end": v(-3301.02, -278.04) * mm});
            skFitSpline(sketch, "E174.0", {"points": [v(-1453.62, -178.53) * mm, v(-1433.67, -185.01) * mm, v(-1397.35, -196.82) * mm, v(-1344.25, -211.67) * mm, v(-1277.2, -220.23) * mm, v(-1193.6, -221.95) * mm, v(-1093.67, -227.48) * mm, v(-993.6, -227.3) * mm, v(-860.29, -228.9) * mm, v(-726.95, -230.88) * mm, v(-560.28, -230.2) * mm, v(-393.6, -232.5) * mm, v(-193.61, -235.45) * mm, v(6.38, -238.87) * mm, v(206.39, -240.25) * mm, v(406.38, -243.3) * mm, v(606.39, -241.71) * mm, v(806.4, -245.03) * mm, v(1006.37, -239.36) * mm, v(1206.39, -240.72) * mm, v(1406.39, -240.93) * mm, v(1606.4, -238.74) * mm, v(1806.38, -235.28) * mm, v(2006.38, -233.3) * mm, v(2206.39, -232.69) * mm, v(2373.07, -231.4) * mm, v(2506.4, -228.55) * mm, v(2606.48, -226.31) * mm, v(2706.62, -219.36) * mm, v(2806.74, -207.3) * mm, v(2906.87, -190.33) * mm, v(2997.36, -170.15) * mm, v(3054.4, -155.63) * mm, v(3078.38, -149.53) * mm]});
            skLineSegment(sketch, "E175.0", {"start": v(327.38, -242.53) * mm, "end": v(327.38, -169.52) * mm});
            skPoint(sketch, "E176.orphan", {"position": v(3078.38, -149.53) * mm});
            skLineSegment(sketch, "E177", {"start": v(-1258.65, -219.93) * mm, "end": v(-1258.65, -204.86) * mm});
            skLineSegment(sketch, "E178", {"start": v(-1453.62, -178.53) * mm, "end": v(327.38, -241.94) * mm});
            skSolve(sketch);
        }
        {
            var Q0;
            Q0=makeQuery(id+"F5.imprint","IMPRINT",FACE,{"disambiguationData":[TD([[makeQuery(id+"F5.imprint","IMPRINT",EDGE,{"derivedFrom":sQuery(id+"F5.wireOp",EDGE,"E168.0")}),-1.0]])]});
            extrude(context, id + "F6", {"entities" : qUnion([Q0]), "endBound" : BoundingType.SYMMETRIC, "depth" : 12 * mm});
        }
        {
            var Q0;
            {var subQ1=sQuery(id+"F0.wireOp",EDGE,"E5");Q0=makeQuery(id+"F0.imprint","IMPRINT",FACE,{"disambiguationData":[TD([[makeQuery(id+"F0.imprint","IMPRINT",EDGE,{"derivedFrom":subQ1}),1.0]])]});}
            cPlane(context, id + "F7", {"entities" : qUnion([Q0]), "cplaneType" : CPlaneType.OFFSET, "offset" : 50 * mm, "width" : 150 * mm, "height" : 150 * mm});
        }
        {
            var Q0;
            Q0=qCreatedBy(id+"F7.planeOp",FACE);
            var sketch = newSketch(context, id + "F8", { "sketchPlane" : qUnion([Q0])});
            skFitSpline(sketch, "E179.0", {"points": [v(-3106.85, -28.36) * mm, v(-3106.84, -36.2) * mm, v(-3106.83, -56.93) * mm, v(-3105.84, -88.16) * mm, v(-3107.71, -120.62) * mm, v(-3102.15, -149.91) * mm, v(-3089.8, -175.72) * mm, v(-3073.13, -199.87) * mm, v(-3055.1, -222.07) * mm, v(-3032.3, -238.62) * mm, v(-3007.38, -252.17) * mm, v(-2977.5, -261.52) * mm, v(-2943.16, -267.16) * mm, v(-2905.31, -272.49) * mm, v(-2866.73, -274.75) * mm, v(-2827.37, -272.89) * mm, v(-2787.99, -272.23) * mm, v(-2748.44, -266.72) * mm, v(-2708.77, -261.2) * mm, v(-2658.88, -254.18) * mm, v(-2600.29, -244.6) * mm, v(-2529.65, -230.59) * mm, v(-2462.65, -217.08) * mm, v(-2398.62, -202.29) * mm, v(-2346.26, -189.92) * mm, v(-2305.08, -177.28) * mm, v(-2275.98, -165.33) * mm, v(-2254.96, -153.28) * mm, v(-2241.28, -138.3) * mm, v(-2229.94, -121.98) * mm, v(-2221.47, -100.85) * mm, v(-2216.66, -76.68) * mm, v(-2216.56, -50.55) * mm, v(-2216.42, -34.2) * mm, v(-2216.34, -25.35) * mm]});
            skFitSpline(sketch, "E180.0", {"points": [v(-2243.05, -25.44) * mm, v(-2243.92, -34.46) * mm, v(-2245.85, -54.63) * mm, v(-2251.34, -85.5) * mm, v(-2265.47, -115.57) * mm, v(-2292.73, -140.08) * mm, v(-2330.98, -148.96) * mm, v(-2371.6, -149.14) * mm, v(-2408.8, -149.35) * mm, v(-2442.96, -151.02) * mm, v(-2475.1, -150.38) * mm, v(-2506.73, -151.37) * mm, v(-2538.59, -155.66) * mm, v(-2566.28, -166.86) * mm, v(-2592.9, -178.47) * mm, v(-2618.54, -191.7) * mm, v(-2644.93, -208.4) * mm, v(-2678.45, -220.34) * mm, v(-2714.3, -230.65) * mm, v(-2753.93, -235.55) * mm, v(-2794.77, -237.78) * mm, v(-2839.22, -241.05) * mm, v(-2883.28, -240.24) * mm, v(-2925.32, -240.48) * mm, v(-2963, -232.2) * mm, v(-2994.87, -223.4) * mm, v(-3020.34, -209.42) * mm, v(-3039.1, -193.65) * mm, v(-3053.59, -174.03) * mm, v(-3068.64, -153.57) * mm, v(-3076.65, -124.92) * mm, v(-3076.77, -90.71) * mm, v(-3075.9, -57.52) * mm, v(-3075.82, -36.07) * mm, v(-3075.8, -27.58) * mm]});
            skLineSegment(sketch, "E181", {"start": v(-3106.85, -28.36) * mm, "end": v(-3075.8, -27.58) * mm});
            skLineSegment(sketch, "E182", {"start": v(-2243.05, -25.44) * mm, "end": v(-2216.34, -25.35) * mm});
            skSolve(sketch);
        }
        {
            var Q0;
            Q0 = qSketchRegion(id + "F8", true);
            extrude(context, id + "F9", {"entities" : qUnion([Q0]), "endBound" : BoundingType.SYMMETRIC, "depth" : 12 * mm});
        }
        {
            var Q0;
            Q0=makeQuery(id+"F3.opExtrude","SWEPT_BODY",BODY,{"disambiguationData":[OSD([sQuery(id+"F2.wireOp",EDGE,"E126.0"),sQuery(id+"F2.wireOp",EDGE,"E126.1"),sQuery(id+"F2.wireOp",EDGE,"E126.2"),sQuery(id+"F2.wireOp",EDGE,"E126.3"),sQuery(id+"F2.wireOp",EDGE,"E126.4"),sQuery(id+"F2.wireOp",EDGE,"E127"),sQuery(id+"F2.wireOp",EDGE,"E128")])]});
            transform(context, id + "F10", {"entities" : qUnion([Q0]), "transformType" : TransformType.TRANSLATION_3D, "dx" : 0 * mm, "dy" : -150 * mm, "dz" : 0 * mm, "makeCopy" : false});
        }
        {
            var Q0;
            Q0=makeQuery(id+"F3.opExtrude","SWEPT_BODY",BODY,{"disambiguationData":[OSD([sQuery(id+"F2.wireOp",EDGE,"E126.0"),sQuery(id+"F2.wireOp",EDGE,"E126.1"),sQuery(id+"F2.wireOp",EDGE,"E126.2"),sQuery(id+"F2.wireOp",EDGE,"E126.3"),sQuery(id+"F2.wireOp",EDGE,"E126.4"),sQuery(id+"F2.wireOp",EDGE,"E127"),sQuery(id+"F2.wireOp",EDGE,"E128")])]});
            var Q1;
            Q1=makeQuery(id+"F3.opExtrude","SWEPT_EDGE",EDGE,{"disambiguationData":[OSD([sQuery(id+"F2.wireOp",EDGE,"E126.4"),sQuery(id+"F2.wireOp",EDGE,"E127")])]});
            transform(context, id + "F11", {"entities" : qUnion([Q0]), "transformType" : TransformType.ROTATION, "transformAxis" : qUnion([Q1]), "angle" : 90 * degree, "oppositeDirection" : true, "makeCopy" : false});
        }
        {
            var Q0;
            Q0=makeQuery(id+"F3.opExtrude","SWEPT_BODY",BODY,{"disambiguationData":[OSD([sQuery(id+"F2.wireOp",EDGE,"E126.0"),sQuery(id+"F2.wireOp",EDGE,"E126.1"),sQuery(id+"F2.wireOp",EDGE,"E126.2"),sQuery(id+"F2.wireOp",EDGE,"E126.3"),sQuery(id+"F2.wireOp",EDGE,"E126.4"),sQuery(id+"F2.wireOp",EDGE,"E127"),sQuery(id+"F2.wireOp",EDGE,"E128")])]});
            var Q1;
            Q1=makeQuery(id+"F3.opExtrude","SWEPT_FACE",FACE,{"disambiguationData":[OSD([sQuery(id+"F2.wireOp",EDGE,"E128")])]});
            mirror(context, id + "F12", {"entities" : qUnion([Q0]), "mirrorPlane" : qUnion([Q1])});
        }
    });
